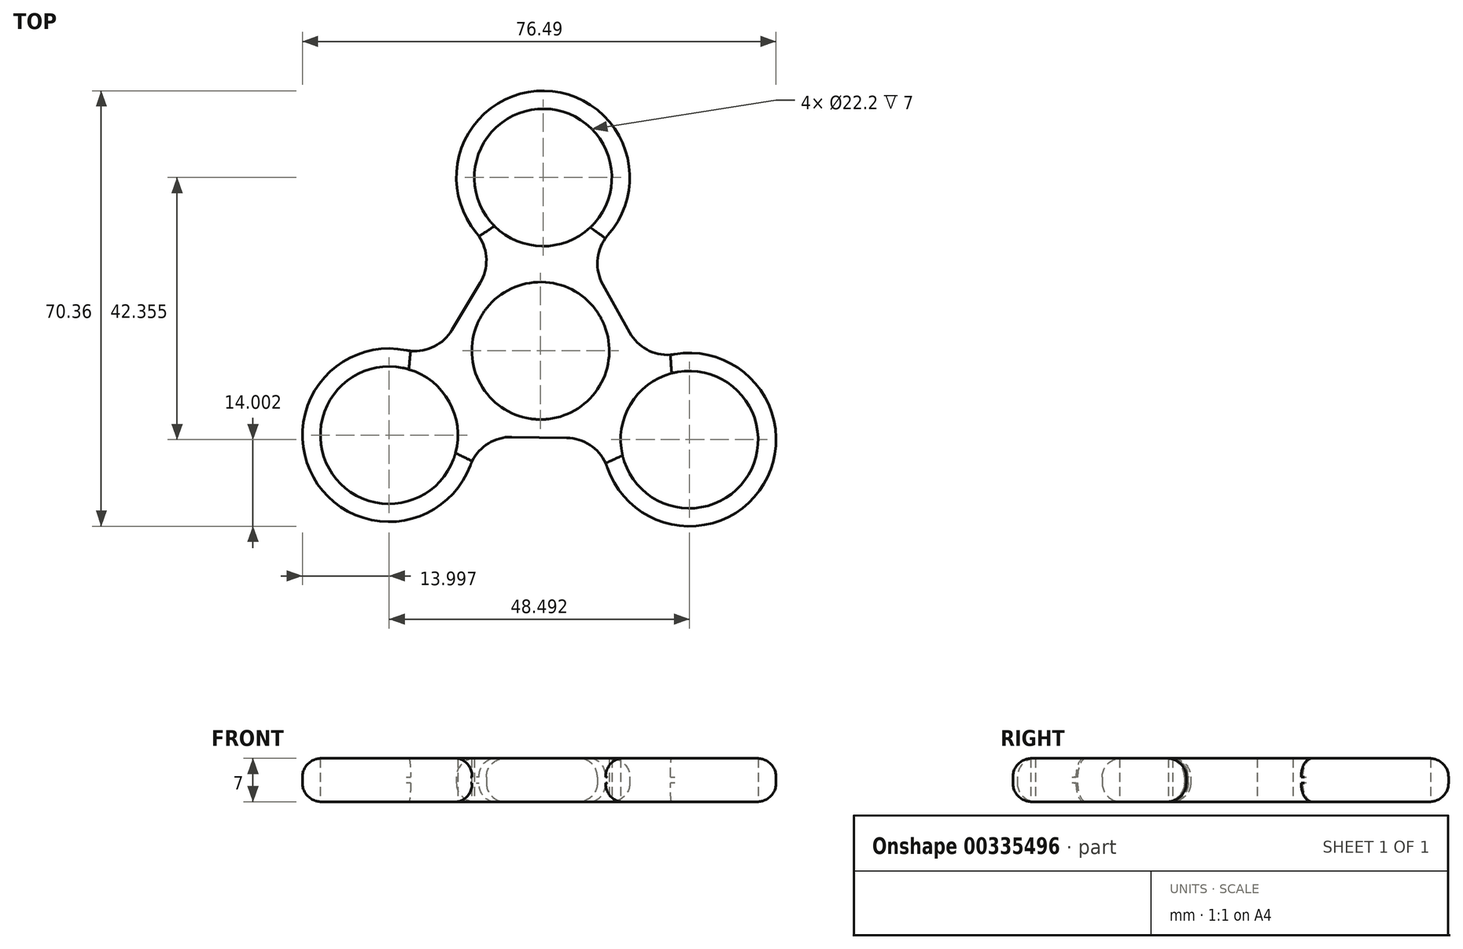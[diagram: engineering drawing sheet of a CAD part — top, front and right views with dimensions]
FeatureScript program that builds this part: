
annotation { "Feature Type Name" : "Feature", "Feature Type Description" : "" }
export const myFeature = defineFeature(function(context is Context, id is Id, definition is map)
    precondition{}
    {
        {
            var Q0;
            Q0=qCreatedBy(makeId("Top.planeOp"),FACE);
            var sketch = newSketch(context, id + "F0", { "sketchPlane" : qUnion([Q0])});
            skCircle(sketch, "E0", {"center": v(0, 0) * mm, "radius": 11.1 * mm});
            skCircle(sketch, "E1.cCircle", {"center": v(0, 0) * mm, "radius": 14 * mm, "construction": true});
            skLineSegment(sketch, "E1.0", {"start": v(0.41, 28) * mm, "end": v(24.04, -14.36) * mm});
            skLineSegment(sketch, "E1.1", {"start": v(24.04, -14.36) * mm, "end": v(-24.45, -13.64) * mm});
            skLineSegment(sketch, "E1.2", {"start": v(-24.45, -13.64) * mm, "end": v(0.41, 28) * mm});
            skPoint(sketch, "E1.0.midPoint", {"position": v(12.23, 6.82) * mm});
            skCircle(sketch, "E2", {"center": v(-24.45, -13.64) * mm, "radius": 11.1 * mm});
            skCircle(sketch, "E3", {"center": v(-24.45, -13.64) * mm, "radius": 14 * mm});
            skCircle(sketch, "E4", {"center": v(24.04, -14.36) * mm, "radius": 11.1 * mm});
            skCircle(sketch, "E5", {"center": v(24.04, -14.36) * mm, "radius": 14 * mm});
            skCircle(sketch, "E6", {"center": v(0.41, 28) * mm, "radius": 11.1 * mm});
            skCircle(sketch, "E7", {"center": v(0.41, 28) * mm, "radius": 14 * mm});
            skSolve(sketch);
        }
        {
            var Q0;
            {var subQ0=sQuery(id+"F0.wireOp",EDGE,"E3");var subQ1=sQuery(id+"F0.wireOp",EDGE,"E1.1");var subQ2=makeQuery(id+"F0.imprint","INTERSECT",VERTEX,{"derivedFrom":[subQ1,subQ0]});Q0=makeQuery(id+"F0.imprint","IMPRINT",FACE,{"disambiguationData":[TD([[makeQuery(id+"F0.imprint","IMPRINT",EDGE,{"disambiguationData":[TD([[subQ2,-1.0]])],"derivedFrom":subQ1}),1.0]])]});}
            var Q1;
            {var subQ0=sQuery(id+"F0.wireOp",EDGE,"E3");var subQ1=sQuery(id+"F0.wireOp",EDGE,"E1.1");var subQ2=makeQuery(id+"F0.imprint","INTERSECT",VERTEX,{"derivedFrom":[subQ1,subQ0]});Q1=makeQuery(id+"F0.imprint","IMPRINT",FACE,{"disambiguationData":[TD([[makeQuery(id+"F0.imprint","IMPRINT",EDGE,{"disambiguationData":[TD([[subQ2,-1.0]])],"derivedFrom":subQ1}),-1.0]])]});}
            var Q2;
            {var subQ0=sQuery(id+"F0.wireOp",EDGE,"E7");var subQ1=sQuery(id+"F0.wireOp",EDGE,"E1.0");var subQ2=makeQuery(id+"F0.imprint","INTERSECT",VERTEX,{"derivedFrom":[subQ1,subQ0]});Q2=makeQuery(id+"F0.imprint","IMPRINT",FACE,{"disambiguationData":[TD([[makeQuery(id+"F0.imprint","IMPRINT",EDGE,{"disambiguationData":[TD([[subQ2,1.0]])],"derivedFrom":subQ1}),1.0]])]});}
            var Q3;
            {var subQ0=sQuery(id+"F0.wireOp",EDGE,"E7");var subQ1=sQuery(id+"F0.wireOp",EDGE,"E1.0");var subQ2=makeQuery(id+"F0.imprint","INTERSECT",VERTEX,{"derivedFrom":[subQ1,subQ0]});Q3=makeQuery(id+"F0.imprint","IMPRINT",FACE,{"disambiguationData":[TD([[makeQuery(id+"F0.imprint","IMPRINT",EDGE,{"disambiguationData":[TD([[subQ2,1.0]])],"derivedFrom":subQ1}),-1.0]])]});}
            var Q4;
            {var subQ0=sQuery(id+"F0.wireOp",EDGE,"E5");var subQ1=sQuery(id+"F0.wireOp",EDGE,"E1.0");var subQ2=makeQuery(id+"F0.imprint","INTERSECT",VERTEX,{"derivedFrom":[subQ1,subQ0]});Q4=makeQuery(id+"F0.imprint","IMPRINT",FACE,{"disambiguationData":[TD([[makeQuery(id+"F0.imprint","IMPRINT",EDGE,{"disambiguationData":[TD([[subQ2,-1.0]])],"derivedFrom":subQ1}),-1.0]])]});}
            var Q5;
            {var subQ0=sQuery(id+"F0.wireOp",EDGE,"E5");var subQ1=sQuery(id+"F0.wireOp",EDGE,"E1.0");var subQ2=makeQuery(id+"F0.imprint","INTERSECT",VERTEX,{"derivedFrom":[subQ1,subQ0]});Q5=makeQuery(id+"F0.imprint","IMPRINT",FACE,{"disambiguationData":[TD([[makeQuery(id+"F0.imprint","IMPRINT",EDGE,{"disambiguationData":[TD([[subQ2,-1.0]])],"derivedFrom":subQ1}),1.0]])]});}
            var Q6;
            Q6=makeQuery(id+"F0.imprint","IMPRINT",FACE,{"disambiguationData":[TD([[makeQuery(id+"F0.imprint","IMPRINT",EDGE,{"derivedFrom":sQuery(id+"F0.wireOp",EDGE,"E0")}),-1.0]])]});
            var Q7;
            Q7=makeQuery(id+"F0.imprint","IMPRINT",FACE,{"disambiguationData":[TD([[makeQuery(id+"F0.imprint","IMPRINT",EDGE,{"derivedFrom":sQuery(id+"F0.wireOp",EDGE,"IE7xh9am-CU8p-DvJk-Ypjl-dGRjJ8XP5DHI")}),-1.0]])]});
            extrude(context, id + "F1", {"entities" : qUnion([Q0, Q1, Q2, Q3, Q4, Q5, Q6, Q7]), "depth" : 7 * mm});
        }
        {
            var Q0;
            Q0=makeQuery(id+"F1.opExtrude","SWEPT_EDGE",EDGE,{"disambiguationData":[OSD([sQuery(id+"F0.wireOp",EDGE,"E1.1"),sQuery(id+"F0.wireOp",EDGE,"E3")])]});
            var Q1;
            Q1=makeQuery(id+"F1.opExtrude","SWEPT_EDGE",EDGE,{"disambiguationData":[OSD([sQuery(id+"F0.wireOp",EDGE,"E1.1"),sQuery(id+"F0.wireOp",EDGE,"E5")])]});
            var Q2;
            Q2=makeQuery(id+"F1.opExtrude","SWEPT_EDGE",EDGE,{"disambiguationData":[OSD([sQuery(id+"F0.wireOp",EDGE,"E1.0"),sQuery(id+"F0.wireOp",EDGE,"E5")])]});
            var Q3;
            Q3=makeQuery(id+"F1.opExtrude","SWEPT_EDGE",EDGE,{"disambiguationData":[OSD([sQuery(id+"F0.wireOp",EDGE,"E1.0"),sQuery(id+"F0.wireOp",EDGE,"E7")])]});
            var Q4;
            Q4=makeQuery(id+"F1.opExtrude","SWEPT_EDGE",EDGE,{"disambiguationData":[OSD([sQuery(id+"F0.wireOp",EDGE,"E1.2"),sQuery(id+"F0.wireOp",EDGE,"E3")])]});
            var Q5;
            Q5=makeQuery(id+"F1.opExtrude","SWEPT_EDGE",EDGE,{"disambiguationData":[OSD([sQuery(id+"F0.wireOp",EDGE,"E1.2"),sQuery(id+"F0.wireOp",EDGE,"E7")])]});
            fillet(context, id + "F2", {"entities" : qUnion([Q0, Q1, Q2, Q3, Q4, Q5]), "radius" : 7 * mm, "tangentPropagation" : true, "allowEdgeOverflow" : false});
        }
        {
            var Q0;
            Q0=makeQuery(id+"F1.opExtrude","CAP_EDGE",EDGE,{"disambiguationData":[OSD([sQuery(id+"F0.wireOp",EDGE,"E7")])],"isStart":false});
            var Q1;
            Q1=makeQuery(id+"F1.opExtrude","CAP_EDGE",EDGE,{"disambiguationData":[OSD([sQuery(id+"F0.wireOp",EDGE,"E7")])],"isStart":true});
            fillet(context, id + "F3", {"entities" : qUnion([Q0, Q1]), "radius" : 3 * mm, "tangentPropagation" : true, "allowEdgeOverflow" : false});
        }
    });
